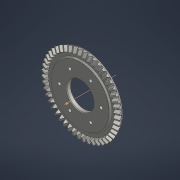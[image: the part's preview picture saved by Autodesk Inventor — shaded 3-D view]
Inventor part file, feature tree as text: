
AUTODESK INVENTOR PART (.ipt)
format: ipt  version: 2022 (Build 260153000, 153)  size: 837,632 bytes
history: native  units: mm
features: other x26, sketch x5, chamfer x4, extrude x3, reference x3, loft x2, pattern_circular x2, plane x2, hole x1, projected_geometry x1
ambient origin geometry x6: Origin, XZ Plane, X Axis, Y Axis, Z Axis, Center Point
bodies: Solid1 (feature_tree)
feature tree (49):
  other  "Top Point"
  other  "Mesh Plane2"
  other  "Teeth Body"
  other  "Start Point"
  other  "Tooth Plane"
  other  "Start Sketch"
  other  "End Point"
  other  "3D Sketch Right"
  other  "End Plane Right"
  loft  "Loft Right"
  pattern_circular  "Circular Pattern Right"  [2 undecoded]
  other  "3D Sketch Left"
  other  "End Plane Left"
  loft  "Loft Left"
  pattern_circular  "Circular Pattern Left"  [2 undecoded]
  other  "Fix Body"
  plane  "Work Plane6"
  extrude  "Extrusion4"  Depth=4.6mm
  sketch  "Sketch17"  dims[d3=8.0mm]
  plane  "Work Plane9"
  extrude  "Extrusion9"  Depth=4.6mm
  chamfer  "Chamfer6"  Distance=50.049398mm
  chamfer  "Chamfer7"  Distance=124.522644mm
  extrude  "Extrusion10"  TaperAngle=0.0deg  [1 undecoded]
  chamfer  "Chamfer8"  Distance=480.0mm Angle=90.0deg
  hole  "Hole2"  [1 undecoded]
  chamfer  "Chamfer9"  Distance=357.584802mm
  other  "Mesh Plane"
  other  "Top Plane"
  other  "Teeth Body Sketch"
  other  "End Plane"
  other  "End Sketch"
  other  "Helical Curve Left"
  other  "End Sketch Left"
  other  "Body Sketch"
  sketch  "Sketch6"  dims[d0=120.0mm d1=118.488225mm]
  other  "Srf1"
  other  "Helical Curve Right"
  other  "End Sketch Right"
  sketch  "Sketch11"  dims[d2=122.536758mm]
  reference  "Reference9"
  reference  "Reference11"
  sketch  "Sketch19"  dims[d4=20.545674mm]
  projected_geometry  "Projected Loop5"
  sketch  "Sketch20"  dims[d5=90.0deg d7=59.301777mm d8=57.411626mm d9=142.839828mm d11=8.275mm d12=51.697165mm d15=50.049398mm d16=124.522644mm d17=0.0mm d18=90.0deg d19=0.0mm d20=90.0deg d21=480.0mm d22=360.0deg d26=357.584802mm d27=3.045601mm d28=120.0mm d29=-11.938871mm d30=51.697165mm d31=50.049398mm d32=124.522644mm d35=0.0mm d37=0.0mm d39=0.0mm d40=90.0deg d41=480.0mm d42=360.0deg d46=90.0deg d47=90.0deg d48=0.0mm d49=0.0mm d50=90.0deg d51=0.654498mm d52=0.0mm d53=0.0mm d54=0.0mm d56=19.770163mm d57=168.118244mm d58=160.308244mm d59=146.559461mm d60=139.750983mm d61=146.559461mm d62=139.750983mm d65=357.584802mm d66=31.5mm d67=120.0mm d68=-11.938871mm d69=3.045601mm d70=50.049398mm d71=124.522644mm d72=51.697165mm d73=139.750983mm d74=146.559461mm d75=0.0mm d77=0.0mm d79=0.0mm d80=90.0deg d81=480.0mm d82=360.0deg d84=10.0mm d85=20.0mm d86=20.0mm d87=10.0mm d88=0.0mm d89=0.0mm d90=90.0deg d91=90.0deg d92=90.0deg d93=90.0deg d103=0.0mm d104=0.0mm d138=42.0mm d139=5.0mm d140=10.0mm d141=0.0mm d142=2.0mm d143=2.0mm d144=45.0deg d145=1.0mm d146=2.0mm d147=45.0deg d148=2.0mm d149=0.0mm d150=2.0mm d151=2.0mm d152=3.490659mm d153=4.5mm d154=5.0mm d155=8.0mm d156=4.6mm d157=90.0deg d158=5.8mm d159=20.594885mm d160=2.0mm d161=2.0mm d162=3.490659mm d106=0.5mm d107=0.872665mm d108=0.5mm d109=0.872665mm d128=1.0mm d129=1.0mm d130=8.8mm d131=0.15mm d132=0.25mm d133=0.375mm d134=14.3117mm d135=6.0mm d136=20.594885mm d137=0.0625mm]
  reference  "Reference13"
  other  "Pitch Diameter"
  other  "Assembly2.iam"
  other  "Tuerca3:1"
note: 6 required parameter values undecoded (feature->parameter linkage not recoverable at this tier; creation-order binding heuristic only, values carry confidence <= 0.55)
